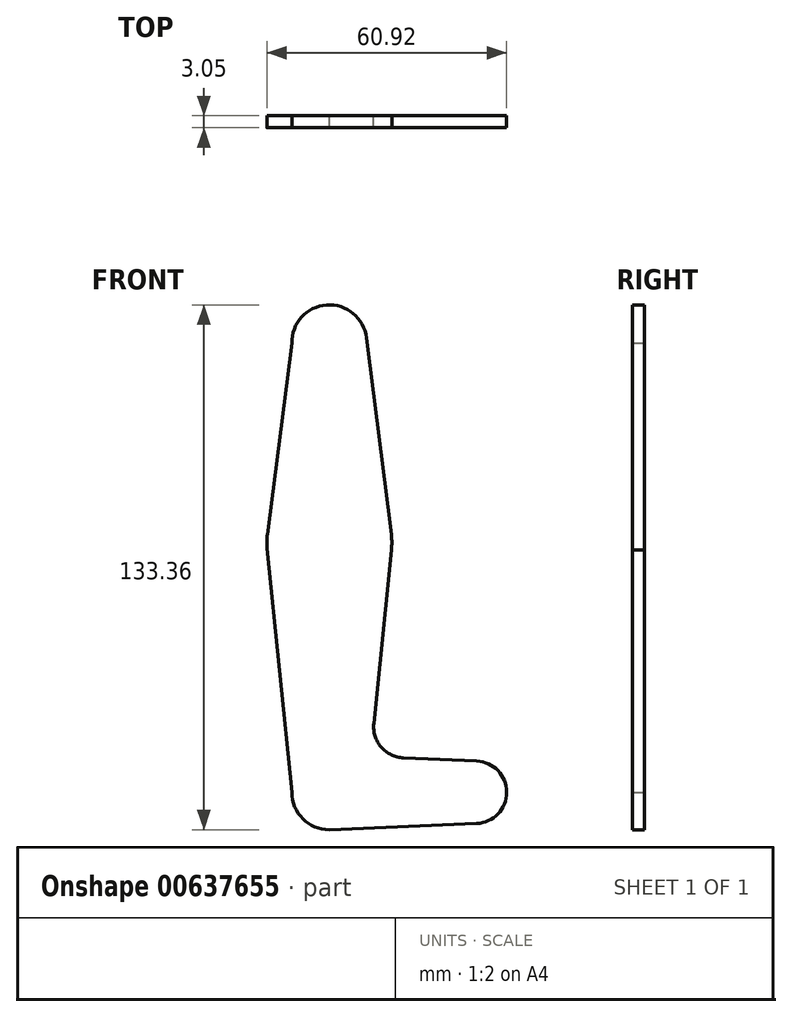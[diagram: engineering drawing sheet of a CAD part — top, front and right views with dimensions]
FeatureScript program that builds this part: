
annotation { "Feature Type Name" : "Feature", "Feature Type Description" : "" }
export const myFeature = defineFeature(function(context is Context, id is Id, definition is map)
    precondition{}
    {
        {
            var Q0;
            Q0=qCreatedBy(makeId("Front.planeOp"),FACE);
            var sketch = newSketch(context, id + "F0", { "sketchPlane" : qUnion([Q0])});
            skLineSegment(sketch, "E0", {"start": v(0, 114.3) * mm, "end": v(0, 0) * mm, "construction": true});
            skLineSegment(sketch, "E1", {"start": v(0, 0) * mm, "end": v(37.11, 0) * mm, "construction": true});
            skCircle(sketch, "E2", {"center": v(0, 114.3) * mm, "radius": 9.53 * mm});
            skCircle(sketch, "E3", {"center": v(0, 0) * mm, "radius": 9.53 * mm});
            skCircle(sketch, "E4", {"center": v(37.11, 0) * mm, "radius": 7.94 * mm});
            skCircle(sketch, "E5", {"center": v(0, 63.5) * mm, "radius": 15.88 * mm});
            skLineSegment(sketch, "E6", {"start": v(-9.52, 114.1) * mm, "end": v(-15.75, 65.52) * mm});
            skLineSegment(sketch, "E7", {"start": v(-9.53, 0) * mm, "end": v(-15.8, 61.9) * mm});
            skLineSegment(sketch, "E8", {"start": v(0, 9.53) * mm, "end": v(0.8, 9.5) * mm});
            skLineSegment(sketch, "E9", {"start": v(0, -9.53) * mm, "end": v(37.45, -7.93) * mm});
            skLineSegment(sketch, "E10.trimOffspring", {"start": v(18.86, 8.72) * mm, "end": v(37.45, 7.93) * mm});
            skLineSegment(sketch, "E11", {"start": v(9.46, 115.45) * mm, "end": v(15.75, 65.48) * mm});
            skLineSegment(sketch, "E12", {"start": v(15.75, 61.52) * mm, "end": v(11.3, 17.47) * mm});
            skCircle(sketch, "E13", {"center": v(0, 114.3) * mm, "radius": 3.18 * mm});
            skCircle(sketch, "E14", {"center": v(0, 63.5) * mm, "radius": 3.18 * mm});
            skCircle(sketch, "E15", {"center": v(-6.35, 99.47) * mm, "radius": 1.59 * mm});
            skPoint(sketch, "E16.visualSharp", {"position": v(10.44, 9.08) * mm});
            skArc(sketch, "E16.filletArc", {"start": v(11.3, 17.47) * mm, "mid": v(13.2, 11.46) * mm, "end": v(18.86, 8.72) * mm});
            skSolve(sketch);
        }
        {
            var Q0;
            {var subQ0=sQuery(id+"F0.wireOp",EDGE,"E4");var subQ1=makeQuery(id+"F0.imprint","INTERSECT",VERTEX,{"derivedFrom":[subQ0,sQuery(id+"F0.wireOp",EDGE,"E9")]});Q0=makeQuery(id+"F0.imprint","IMPRINT",FACE,{"disambiguationData":[TD([[makeQuery(id+"F0.imprint","IMPRINT",EDGE,{"disambiguationData":[TD([[subQ1,1.0]])],"derivedFrom":subQ0}),1.0]])]});}
            var Q1;
            {var subQ0=sQuery(id+"F0.wireOp",EDGE,"E6");Q1=makeQuery(id+"F0.imprint","IMPRINT",FACE,{"disambiguationData":[TD([[makeQuery(id+"F0.imprint","IMPRINT",EDGE,{"derivedFrom":subQ0}),1.0]])]});}
            var Q2;
            Q2=makeQuery(id+"F0.imprint","IMPRINT",FACE,{"disambiguationData":[TD([[makeQuery(id+"F0.imprint","IMPRINT",EDGE,{"derivedFrom":sQuery(id+"F0.wireOp",EDGE,"E14")}),-1.0]])]});
            var Q3;
            Q3=makeQuery(id+"F0.imprint","IMPRINT",FACE,{"disambiguationData":[TD([[makeQuery(id+"F0.imprint","IMPRINT",EDGE,{"derivedFrom":sQuery(id+"F0.wireOp",EDGE,"E13")}),-1.0]])]});
            var Q4;
            {var subQ7=sQuery(id+"F0.wireOp",EDGE,"E7");Q4=makeQuery(id+"F0.imprint","IMPRINT",FACE,{"disambiguationData":[TD([[makeQuery(id+"F0.imprint","IMPRINT",EDGE,{"derivedFrom":subQ7}),-1.0]])]});}
            var Q5;
            Q5=makeQuery(id+"F0.imprint","IMPRINT",FACE,{"disambiguationData":[TD([[makeQuery(id+"F0.imprint","IMPRINT",EDGE,{"derivedFrom":sQuery(id+"F0.wireOp",EDGE,"E14")}),1.0]])]});
            var Q6;
            Q6=makeQuery(id+"F0.imprint","IMPRINT",FACE,{"disambiguationData":[TD([[makeQuery(id+"F0.imprint","IMPRINT",EDGE,{"derivedFrom":sQuery(id+"F0.wireOp",EDGE,"E15")}),1.0]])]});
            var Q7;
            {var subQ0=sQuery(id+"F0.wireOp",EDGE,"E8");Q7=makeQuery(id+"F0.imprint","IMPRINT",FACE,{"disambiguationData":[TD([[makeQuery(id+"F0.imprint","IMPRINT",EDGE,{"derivedFrom":subQ0}),-1.0]])]});}
            var Q8;
            {var subQ0=sQuery(id+"F0.wireOp",EDGE,"E9");var subQ1=sQuery(id+"F0.wireOp",EDGE,"E3");var subQ2=makeQuery(id+"F0.imprint","INTERSECT",VERTEX,{"disambiguationData":[OD(0.0)],"derivedFrom":[subQ1,subQ0]});Q8=makeQuery(id+"F0.imprint","IMPRINT",FACE,{"disambiguationData":[TD([[makeQuery(id+"F0.imprint","IMPRINT",EDGE,{"disambiguationData":[TD([[subQ2,-1.0]])],"derivedFrom":subQ1}),1.0]])]});}
            var Q9;
            {var subQ0=sQuery(id+"F0.wireOp",EDGE,"E8");Q9=makeQuery(id+"F0.imprint","IMPRINT",FACE,{"disambiguationData":[TD([[makeQuery(id+"F0.imprint","IMPRINT",EDGE,{"derivedFrom":subQ0}),1.0]])]});}
            var Q10;
            Q10=makeQuery(id+"F0.imprint","IMPRINT",FACE,{"disambiguationData":[TD([[makeQuery(id+"F0.imprint","IMPRINT",EDGE,{"derivedFrom":sQuery(id+"F0.wireOp",EDGE,"E13")}),1.0]])]});
            extrude(context, id + "F1", {"entities" : qUnion([Q0, Q1, Q2, Q3, Q4, Q5, Q6, Q7, Q8, Q9, Q10]), "depth" : 3.05 * mm, "offsetDistance" : 25.4 * mm});
        }
    });
